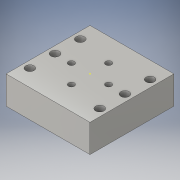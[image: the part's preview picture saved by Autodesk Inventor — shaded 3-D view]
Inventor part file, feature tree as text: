
AUTODESK INVENTOR PART (.ipt)
format: ipt  version: 2016 (Build 200138000, 138)  size: 182,784 bytes
history: native  units: mm
features: sketch x4, hole x2, projected_geometry x2, extrude x1
ambient origin geometry x8: Origin, YZ Plane, XZ Plane, XY Plane, X Axis, Y Axis, Z Axis, Center Point
bodies: Solid1 (feature_tree)
feature tree (9):
  extrude  "Extrusion1"  Depth=3.175mm
  sketch  "Sketch4"  dims[d46=31.75mm d47=22.86mm d48=22.86mm d49=31.75mm d50=11.938mm d51=11.938mm d52=16.882882mm d53=16.882882mm d54=4.445mm d55=7.433559mm d56=5.969mm d57=5.969mm d58=4.445mm d59=7.433559mm d60=9.906mm d61=9.906mm d62=21.844mm d63=21.844mm d64=3.175mm d65=3.175mm]
  hole  "Hole2"  [1 undecoded]
  hole  "Hole3"  [1 undecoded]
  sketch  "Sketch5"  dims[d66=3.7973mm d67=19.05mm d68=9.525mm d69=6.35mm d70=14.3117mm d71=25.4mm d72=20.594885mm]
  projected_geometry  "Projected Loop3"
  sketch  "Sketch6"  dims[d73=31.75mm d74=22.86mm d75=22.86mm d76=31.75mm d77=11.938mm d78=11.938mm d79=16.882882mm d80=16.882882mm d81=4.445mm d82=7.433559mm d83=5.969mm d84=5.969mm d85=4.445mm d86=7.433559mm d87=9.906mm d88=9.906mm d89=21.844mm d90=21.844mm d91=3.175mm d92=3.175mm d93=2.7051mm d94=12.7mm d95=9.525mm d96=6.35mm d97=14.3117mm d98=6.35mm d99=20.594885mm]
  projected_geometry  "Projected Loop4"
  sketch  "Sketch1"  dims[d0=38.1mm d1=38.1mm d3=0.0mm d4=12.7mm]
note: 2 required parameter values undecoded (feature->parameter linkage not recoverable at this tier; creation-order binding heuristic only, values carry confidence <= 0.55)
